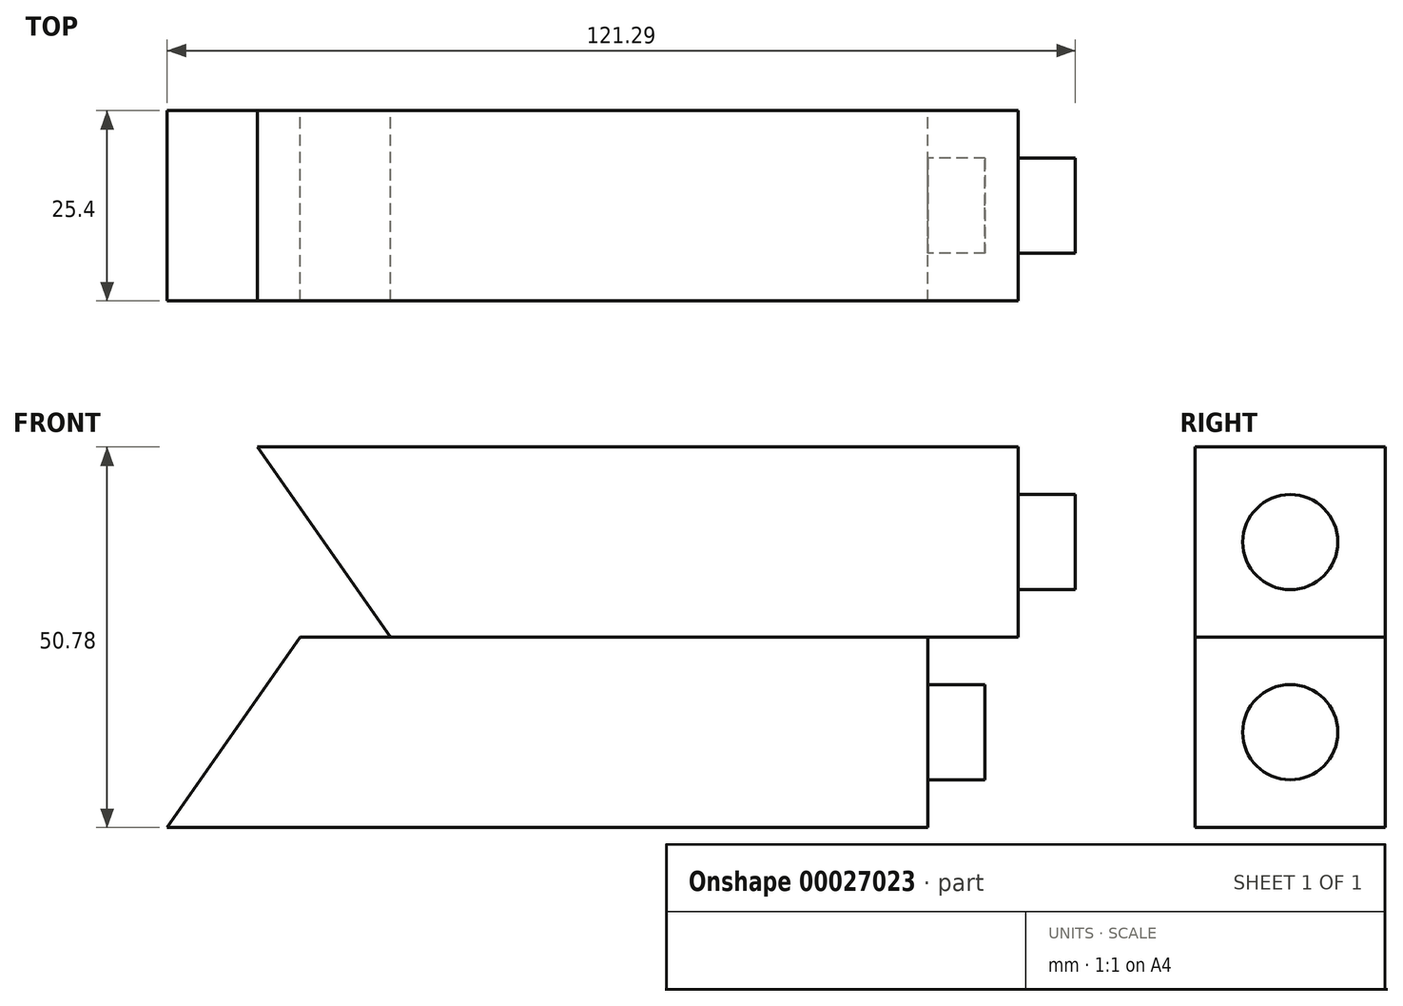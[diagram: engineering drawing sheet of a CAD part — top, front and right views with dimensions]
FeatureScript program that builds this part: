
annotation { "Feature Type Name" : "Feature", "Feature Type Description" : "" }
export const myFeature = defineFeature(function(context is Context, id is Id, definition is map)
    precondition{}
    {
        {
            var Q0;
            Q0=qCreatedBy(makeId("Front.planeOp"),FACE);
            var sketch = newSketch(context, id + "F0", { "sketchPlane" : qUnion([Q0])});
            skLineSegment(sketch, "E0", {"start": v(-34.25, 37.05) * mm, "end": v(61, 37.05) * mm});
            skPoint(sketch, "E1.orphan", {"position": v(-34.25, 62.45) * mm});
            skLineSegment(sketch, "E2.MirrorCS", {"start": v(-34.25, 37.05) * mm, "end": v(-16.47, 11.65) * mm});
            skPoint(sketch, "E3.MirrorP", {"position": v(-34.25, 11.65) * mm});
            skLineSegment(sketch, "E4.MirrorCS", {"start": v(-16.47, 11.65) * mm, "end": v(-34.25, 37.05) * mm});
            skLineSegment(sketch, "E5.MirrorCS", {"start": v(67.35, 11.65) * mm, "end": v(67.35, 30.7) * mm});
            skLineSegment(sketch, "E6.MirrorCS", {"start": v(-16.47, 11.65) * mm, "end": v(67.35, 11.65) * mm});
            skPoint(sketch, "E7.right.start.orphan", {"position": v(67.35, 62.45) * mm});
            skPoint(sketch, "E8.start.orphan", {"position": v(67.35, 43.4) * mm});
            skPoint(sketch, "E9.end.orphan", {"position": v(-16.47, 62.45) * mm});
            skLineSegment(sketch, "E10", {"start": v(67.35, 30.7) * mm, "end": v(67.35, 37.05) * mm});
            skLineSegment(sketch, "E11", {"start": v(61, 37.05) * mm, "end": v(67.35, 37.05) * mm});
            skPoint(sketch, "E12.MirrorCS.end.orphan", {"position": v(61, 37.05) * mm});
            skSolve(sketch);
        }
        {
            var Q0;
            Q0=makeQuery(id+"F0.imprint","IMPRINT",FACE,{"disambiguationData":[TD([[makeQuery(id+"F0.imprint","IMPRINT",EDGE,{"derivedFrom":sQuery(id+"F0.wireOp",EDGE,"E0")}),-1.0]])]});
            extrude(context, id + "F1", {"entities" : qUnion([Q0]), "depth" : 25.4 * mm});
        }
        {
            var Q0;
            Q0=qCreatedBy(makeId("Front.planeOp"),FACE);
            var sketch = newSketch(context, id + "F2", { "sketchPlane" : qUnion([Q0])});
            skLineSegment(sketch, "E13.bottom", {"start": v(-28.54, 11.67) * mm, "end": v(55.28, 11.67) * mm});
            skLineSegment(sketch, "E13.right", {"start": v(55.28, 11.67) * mm, "end": v(55.28, -7.38) * mm});
            skLineSegment(sketch, "E14", {"start": v(-46.32, -13.73) * mm, "end": v(-28.54, 11.67) * mm});
            skLineSegment(sketch, "E15", {"start": v(-28.54, 11.67) * mm, "end": v(-46.32, -13.73) * mm});
            skLineSegment(sketch, "E16", {"start": v(-46.32, -13.73) * mm, "end": v(48.93, -13.73) * mm});
            skPoint(sketch, "E17.orphan", {"position": v(-46.32, 11.67) * mm});
            skLineSegment(sketch, "E18", {"start": v(55.28, -7.38) * mm, "end": v(55.28, -13.73) * mm});
            skLineSegment(sketch, "E19", {"start": v(48.93, -13.73) * mm, "end": v(55.28, -13.73) * mm});
            skSolve(sketch);
        }
        {
            var Q0;
            Q0=makeQuery(id+"F2.imprint","IMPRINT",FACE,{"disambiguationData":[TD([[makeQuery(id+"F2.imprint","IMPRINT",EDGE,{"derivedFrom":sQuery(id+"F2.wireOp",EDGE,"E13.bottom")}),-1.0]])]});
            extrude(context, id + "F3", {"entities" : qUnion([Q0]), "depth" : 25.4 * mm});
        }
        {
            var Q0;
            Q0=makeQuery(id+"F1.opExtrude","SWEPT_FACE",FACE,{"disambiguationData":[OSD([sQuery(id+"F0.wireOp",EDGE,"E5.MirrorCS"),sQuery(id+"F0.wireOp",EDGE,"E10")])]});
            var sketch = newSketch(context, id + "F4", { "sketchPlane" : qUnion([Q0])});
            skPoint(sketch, "E20", {"position": v(-12.7, 24.35) * mm});
            skCircle(sketch, "E21", {"center": v(-12.7, 24.35) * mm, "radius": 6.35 * mm});
            skSolve(sketch);
        }
        {
            var Q0;
            Q0=makeQuery(id+"F3.opExtrude","SWEPT_FACE",FACE,{"disambiguationData":[OSD([sQuery(id+"F2.wireOp",EDGE,"E13.right"),sQuery(id+"F2.wireOp",EDGE,"E18")])]});
            var sketch = newSketch(context, id + "F5", { "sketchPlane" : qUnion([Q0])});
            skPoint(sketch, "E22", {"position": v(-12.7, -1.03) * mm});
            skCircle(sketch, "E23", {"center": v(-12.7, -1.03) * mm, "radius": 6.35 * mm});
            skSolve(sketch);
        }
        {
            var Q0;
            Q0=makeQuery(id+"F5.imprint","IMPRINT",FACE,{"disambiguationData":[TD([[makeQuery(id+"F5.imprint","IMPRINT",EDGE,{"derivedFrom":sQuery(id+"F5.wireOp",EDGE,"E23")}),1.0]])]});
            extrude(context, id + "F6", {"entities" : qUnion([Q0]), "operationType" : NewBodyOperationType.ADD, "depth" : 7.62 * mm});
        }
        {
            var Q0;
            Q0=makeQuery(id+"F4.imprint","IMPRINT",FACE,{"disambiguationData":[TD([[makeQuery(id+"F4.imprint","IMPRINT",EDGE,{"derivedFrom":sQuery(id+"F4.wireOp",EDGE,"E21")}),1.0]])]});
            extrude(context, id + "F7", {"entities" : qUnion([Q0]), "operationType" : NewBodyOperationType.ADD, "depth" : 7.62 * mm});
        }
    });
